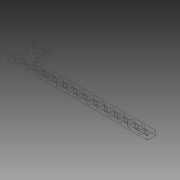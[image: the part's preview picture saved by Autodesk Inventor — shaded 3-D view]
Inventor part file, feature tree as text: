
AUTODESK INVENTOR PART (.ipt)
format: ipt  version: 2012 (Build 160160000, 160)  size: 142,848 bytes
history: native  units: mm
features: extrude x2, sketch x2
ambient origin geometry x8: Origin, YZ Plane, XZ Plane, XY Plane, X Axis, Y Axis, Z Axis, Center Point
bodies: Solid1 (feature_tree)
feature tree (4):
  extrude  "Extrusion1"  Depth=60.0mm
  extrude  "Extrusion2"  Depth=40.0mm
  sketch  "Sketch1"  dims[d0=330.0mm d1=60.0mm]
  sketch  "Sketch2"  dims[d2=42.0mm d3=40.0mm d4=4.1mm d5=24.0mm d6=16.0mm d7=6.0mm d8=9.0mm d9=5.0mm d10=5.0mm d11=10.0mm d12=0.0mm d13=10.0mm d14=12.0mm d15=4.0mm d16=12.0mm d17=12.0mm d18=130.0mm d20=24.0mm d21=10.0mm d23=10.0mm d25=10.0mm d26=0.0mm]
